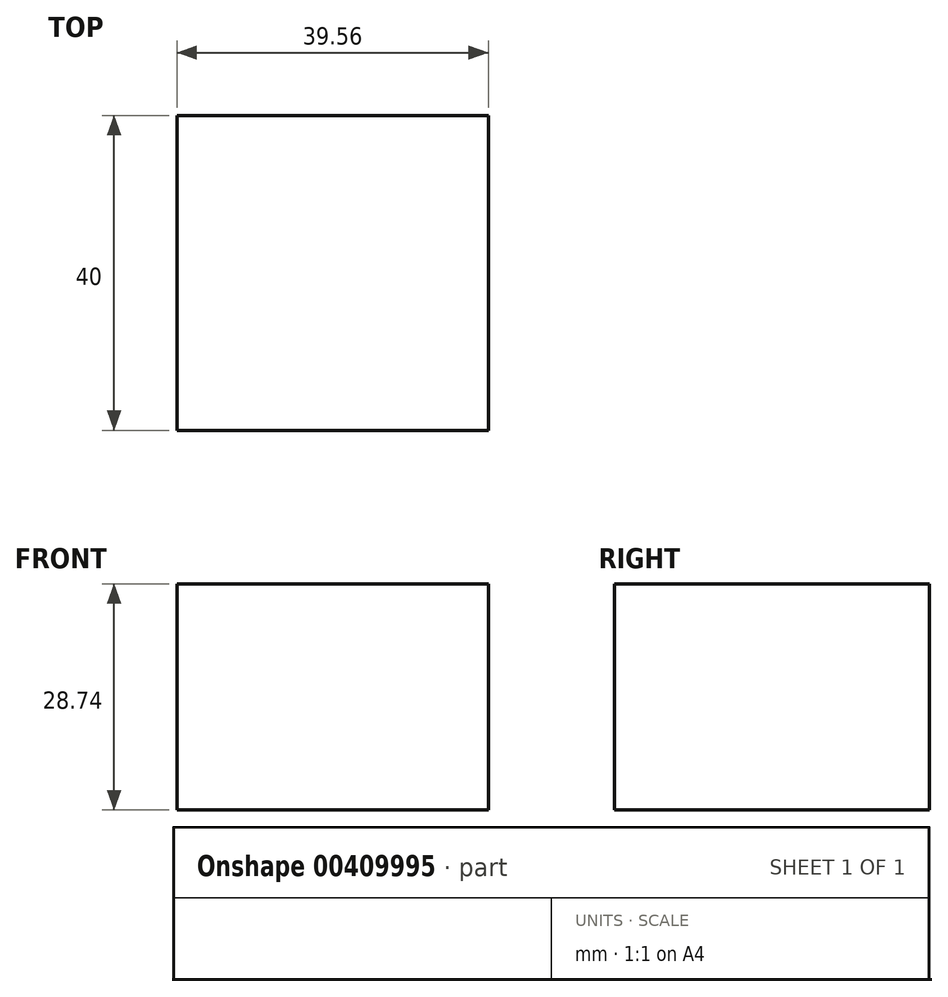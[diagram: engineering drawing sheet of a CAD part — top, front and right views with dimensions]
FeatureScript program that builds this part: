
annotation { "Feature Type Name" : "Feature", "Feature Type Description" : "" }
export const myFeature = defineFeature(function(context is Context, id is Id, definition is map)
    precondition{}
    {
        {
            var Q0;
            Q0=qCreatedBy(makeId("Front.planeOp"),FACE);
            var sketch = newSketch(context, id + "F0", { "sketchPlane" : qUnion([Q0])});
            skLineSegment(sketch, "E0.bottom", {"start": v(-19.78, 14.37) * mm, "end": v(19.78, 14.37) * mm});
            skLineSegment(sketch, "E0.top", {"start": v(-19.78, -14.37) * mm, "end": v(19.78, -14.37) * mm});
            skLineSegment(sketch, "E0.left", {"start": v(-19.78, 14.37) * mm, "end": v(-19.78, -14.37) * mm});
            skLineSegment(sketch, "E0.right", {"start": v(19.78, 14.37) * mm, "end": v(19.78, -14.37) * mm});
            skSolve(sketch);
        }
        {
            var Q0;
            Q0=makeQuery(id+"F0.imprint","IMPRINT",FACE,{"disambiguationData":[TD([[makeQuery(id+"F0.imprint","IMPRINT",EDGE,{"derivedFrom":sQuery(id+"F0.wireOp",EDGE,"E0.bottom")}),-1.0]])]});
            extrude(context, id + "F1", {"entities" : qUnion([Q0]), "oppositeDirection" : true, "depth" : 40 * mm});
        }
    });
